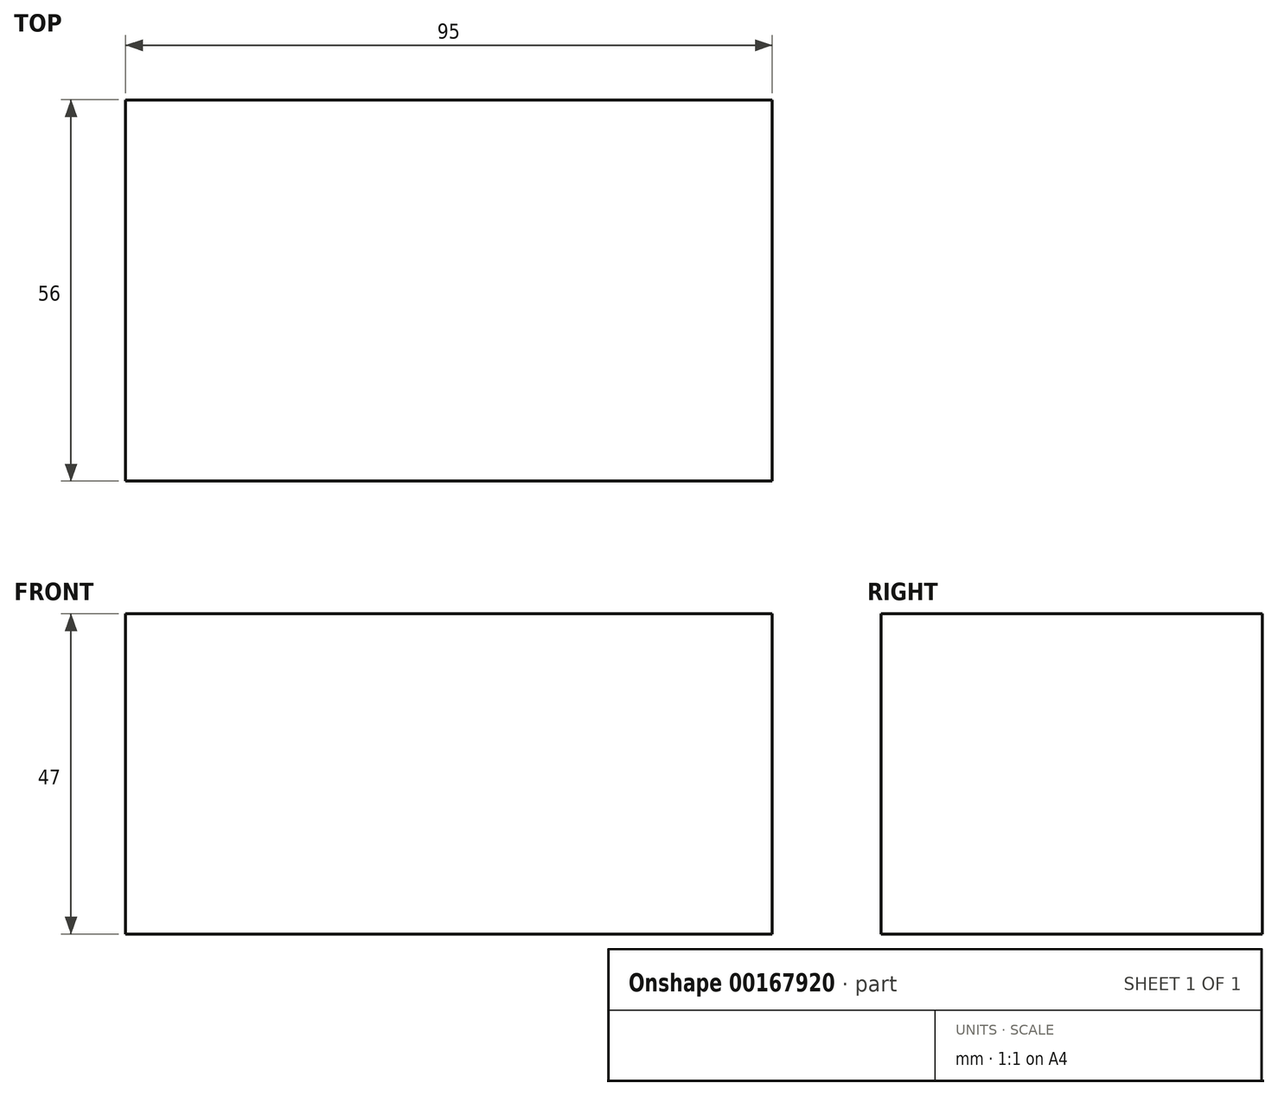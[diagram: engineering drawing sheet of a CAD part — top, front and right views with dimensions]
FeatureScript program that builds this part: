
annotation { "Feature Type Name" : "Feature", "Feature Type Description" : "" }
export const myFeature = defineFeature(function(context is Context, id is Id, definition is map)
    precondition{}
    {
        {
            var Q0;
            Q0=qCreatedBy(makeId("Top.planeOp"),FACE);
            var sketch = newSketch(context, id + "F0", { "sketchPlane" : qUnion([Q0])});
            skLineSegment(sketch, "E0.bottom", {"start": v(-85.3, 60.23) * mm, "end": v(9.7, 60.23) * mm});
            skLineSegment(sketch, "E0.top", {"start": v(-85.3, 4.23) * mm, "end": v(9.7, 4.23) * mm});
            skLineSegment(sketch, "E0.left", {"start": v(-85.3, 60.23) * mm, "end": v(-85.3, 4.23) * mm});
            skLineSegment(sketch, "E0.right", {"start": v(9.7, 60.23) * mm, "end": v(9.7, 4.23) * mm});
            skSolve(sketch);
        }
        {
            var Q0;
            Q0 = qSketchRegion(id + "F0", true);
            extrude(context, id + "F1", {"entities" : qUnion([Q0]), "depth" : 47 * mm});
        }
    });
